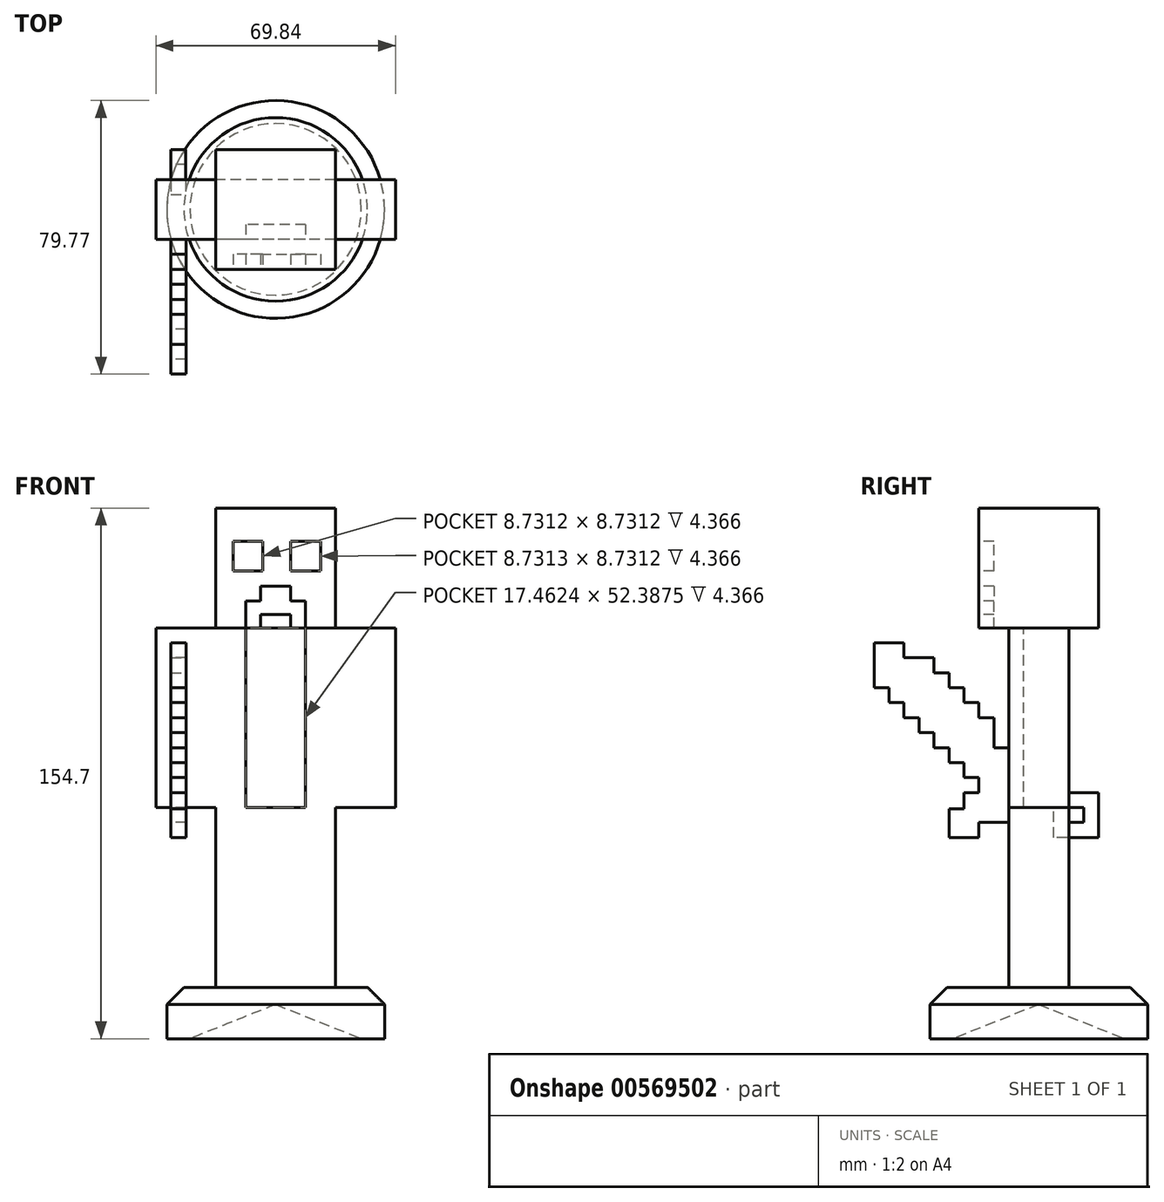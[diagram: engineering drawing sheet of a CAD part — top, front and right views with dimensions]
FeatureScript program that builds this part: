
annotation { "Feature Type Name" : "Feature", "Feature Type Description" : "" }
export const myFeature = defineFeature(function(context is Context, id is Id, definition is map)
    precondition{}
    {
        {
            var Q0;
            Q0=qCreatedBy(makeId("Top.planeOp"),FACE);
            var sketch = newSketch(context, id + "F0", { "sketchPlane" : qUnion([Q0])});
            skCircle(sketch, "E0", {"center": v(0, 0) * mm, "radius": 31.75 * mm});
            skSolve(sketch);
        }
        {
            var Q0;
            Q0=makeQuery(id+"F0.imprint","IMPRINT",FACE,{"disambiguationData":[TD([[makeQuery(id+"F0.imprint","IMPRINT",EDGE,{"derivedFrom":sQuery(id+"F0.wireOp",EDGE,"E0")}),1.0]])]});
            extrude(context, id + "F1", {"entities" : qUnion([Q0]), "depth" : 15 * mm});
        }
        {
            var Q0;
            Q0=makeQuery(id+"F1.opExtrude","CAP_EDGE",EDGE,{"disambiguationData":[OSD([sQuery(id+"F0.wireOp",EDGE,"E0")])],"isStart":false});
            chamfer(context, id + "F2", {"entities" : qUnion([Q0]), "width" : 5 * mm, "tangentPropagation" : true});
        }
        {
            var Q0;
            Q0=makeQuery(id+"F1.opExtrude","CAP_FACE",FACE,{"disambiguationData":[OSD([sQuery(id+"F0.wireOp",EDGE,"E0")])],"isStart":true});
            var sketch = newSketch(context, id + "F3", { "sketchPlane" : qUnion([Q0])});
            skCircle(sketch, "E1", {"center": v(0, 0) * mm, "radius": 25 * mm});
            skSolve(sketch);
        }
        {
            var Q0;
            Q0=makeQuery(id+"F3.imprint","IMPRINT",FACE,{"disambiguationData":[TD([[makeQuery(id+"F3.imprint","IMPRINT",EDGE,{"derivedFrom":sQuery(id+"F3.wireOp",EDGE,"E1")}),1.0]])]});
            extrude(context, id + "F4", {"entities" : qUnion([Q0]), "operationType" : NewBodyOperationType.REMOVE, "oppositeDirection" : true, "depth" : 10 * mm});
        }
        {
            var Q0;
            Q0=makeQuery(id+"F4.boolean.opBoolean","COPY",EDGE,{"derivedFrom":makeQuery(id+"F4.opExtrude","CAP_EDGE",EDGE,{"disambiguationData":[OSD([sQuery(id+"F3.wireOp",EDGE,"E1")])],"isStart":false})});
            chamfer(context, id + "F5", {"entities" : qUnion([Q0]), "chamferType" : ChamferType.TWO_OFFSETS, "width1" : 25 * mm, "oppositeDirection" : false, "width2" : 10 * mm, "tangentPropagation" : true});
        }
        {
            var Q0;
            Q0=makeQuery(id+"F1.opExtrude","CAP_FACE",FACE,{"disambiguationData":[OSD([sQuery(id+"F0.wireOp",EDGE,"E0")])],"isStart":false});
            var sketch = newSketch(context, id + "F6", { "sketchPlane" : qUnion([Q0])});
            skLineSegment(sketch, "E2.bottom", {"start": v(17.46, 8.73) * mm, "end": v(-17.46, 8.73) * mm});
            skLineSegment(sketch, "E2.top", {"start": v(17.46, -8.73) * mm, "end": v(-17.46, -8.73) * mm});
            skLineSegment(sketch, "E2.left", {"start": v(17.46, 8.73) * mm, "end": v(17.46, -8.73) * mm});
            skLineSegment(sketch, "E2.right", {"start": v(-17.46, 8.73) * mm, "end": v(-17.46, -8.73) * mm});
            skPoint(sketch, "E2.middle", {"position": v(0, 0) * mm});
            skSolve(sketch);
        }
        {
            var Q0;
            Q0=makeQuery(id+"F6.imprint","IMPRINT",FACE,{"disambiguationData":[TD([[makeQuery(id+"F6.imprint","IMPRINT",EDGE,{"derivedFrom":sQuery(id+"F6.wireOp",EDGE,"E2.bottom")}),1.0]])]});
            extrude(context, id + "F7", {"entities" : qUnion([Q0]), "operationType" : NewBodyOperationType.ADD, "depth" : 104.77 * mm});
        }
        {
            var Q0;
            Q0=makeQuery(id+"F7.opExtrude","SWEPT_FACE",FACE,{"disambiguationData":[OSD([sQuery(id+"F6.wireOp",EDGE,"E2.right")])]});
            var sketch = newSketch(context, id + "F8", { "sketchPlane" : qUnion([Q0])});
            skSolve(sketch);
        }
        {
            var Q0;
            Q0=makeQuery(id+"F7.opExtrude","SWEPT_FACE",FACE,{"disambiguationData":[OSD([sQuery(id+"F6.wireOp",EDGE,"E2.top")])]});
            var sketch = newSketch(context, id + "F9", { "sketchPlane" : qUnion([Q0])});
            skLineSegment(sketch, "E3", {"start": v(-17.46, 119.77) * mm, "end": v(17.46, 119.77) * mm});
            skSolve(sketch);
        }
        {
            var Q0;
            Q0=makeQuery(id+"F7.opExtrude","CAP_FACE",FACE,{"disambiguationData":[OSD([sQuery(id+"F6.wireOp",EDGE,"E2.bottom"),sQuery(id+"F6.wireOp",EDGE,"E2.top"),sQuery(id+"F6.wireOp",EDGE,"E2.left"),sQuery(id+"F6.wireOp",EDGE,"E2.right")])],"isStart":false});
            var sketch = newSketch(context, id + "F10", { "sketchPlane" : qUnion([Q0])});
            skLineSegment(sketch, "E4.bottom", {"start": v(17.46, -17.46) * mm, "end": v(-17.46, -17.46) * mm});
            skLineSegment(sketch, "E4.top", {"start": v(17.46, 17.46) * mm, "end": v(-17.46, 17.46) * mm});
            skLineSegment(sketch, "E4.left", {"start": v(17.46, -17.46) * mm, "end": v(17.46, 17.46) * mm});
            skLineSegment(sketch, "E4.right", {"start": v(-17.46, -17.46) * mm, "end": v(-17.46, 17.46) * mm});
            skPoint(sketch, "E4.middle", {"position": v(0, 0) * mm});
            skSolve(sketch);
        }
        {
            var Q0;
            Q0=qSketchRegion(id+"F10",true);
            extrude(context, id + "F11", {"entities" : qUnion([Q0]), "operationType" : NewBodyOperationType.ADD, "depth" : 34.92 * mm});
        }
        {
            var Q0;
            Q0=makeQuery(id+"F11.boolean.opBoolean","MERGE",FACE,{"derivedFrom":[makeQuery(id+"F7.opExtrude","SWEPT_FACE",FACE,{"disambiguationData":[OSD([sQuery(id+"F6.wireOp",EDGE,"E2.left")])]}),makeQuery(id+"F11.opExtrude","SWEPT_FACE",FACE,{"disambiguationData":[OSD([sQuery(id+"F10.wireOp",EDGE,"E4.left")])]})]});
            var sketch = newSketch(context, id + "F12", { "sketchPlane" : qUnion([Q0])});
            skLineSegment(sketch, "E5.bottom", {"start": v(-8.73, 119.77) * mm, "end": v(8.73, 119.77) * mm});
            skLineSegment(sketch, "E5.top", {"start": v(-8.73, 102.31) * mm, "end": v(8.73, 102.31) * mm});
            skLineSegment(sketch, "E5.left", {"start": v(-8.73, 119.77) * mm, "end": v(-8.73, 102.31) * mm});
            skLineSegment(sketch, "E5.right", {"start": v(8.73, 119.77) * mm, "end": v(8.73, 102.31) * mm});
            skSolve(sketch);
        }
        {
            var Q0;
            Q0=makeQuery(id+"F12.imprint","IMPRINT",FACE,{"disambiguationData":[TD([[makeQuery(id+"F12.imprint","IMPRINT",EDGE,{"derivedFrom":sQuery(id+"F12.wireOp",EDGE,"E5.bottom")}),-1.0]])]});
            extrude(context, id + "F13", {"entities" : qUnion([Q0]), "operationType" : NewBodyOperationType.ADD, "depth" : 17.46 * mm});
        }
        {
            var Q0;
            Q0=makeQuery(id+"F13.opExtrude","SWEPT_FACE",FACE,{"disambiguationData":[OSD([sQuery(id+"F12.wireOp",EDGE,"E5.top")])]});
            extrude(context, id + "F14", {"entities" : qUnion([Q0]), "operationType" : NewBodyOperationType.ADD, "depth" : 34.92 * mm});
        }
        {
            var Q0;
            {var subQ0=sQuery(id+"F6.wireOp",EDGE,"E2.right");Q0=makeQuery(id+"F8.imprint","IMPRINT",FACE,{"disambiguationData":[TD([[makeQuery(id+"F8.imprint","IMPRINT",EDGE,{"derivedFrom":makeQuery(id+"F7.opExtrude","CAP_EDGE",EDGE,{"disambiguationData":[OSD([subQ0])],"isStart":false})}),-1.0]])]});}
            var sketch = newSketch(context, id + "F15", { "sketchPlane" : qUnion([Q0])});
            skLineSegment(sketch, "E6.bottom", {"start": v(-8.73, 119.77) * mm, "end": v(8.73, 119.77) * mm});
            skLineSegment(sketch, "E6.top", {"start": v(-8.73, 102.31) * mm, "end": v(8.73, 102.31) * mm});
            skLineSegment(sketch, "E6.left", {"start": v(-8.73, 119.77) * mm, "end": v(-8.73, 102.31) * mm});
            skLineSegment(sketch, "E6.right", {"start": v(8.73, 119.77) * mm, "end": v(8.73, 102.31) * mm});
            skLineSegment(sketch, "E7", {"start": v(8.73, 102.31) * mm, "end": v(-8.73, 102.31) * mm});
            skLineSegment(sketch, "E8", {"start": v(-8.73, 102.31) * mm, "end": v(-8.73, 67.39) * mm});
            skLineSegment(sketch, "E9", {"start": v(-8.73, 67.39) * mm, "end": v(8.73, 67.39) * mm});
            skLineSegment(sketch, "E10", {"start": v(8.73, 67.39) * mm, "end": v(8.73, 102.31) * mm});
            skSolve(sketch);
        }
        {
            var Q0;
            Q0=qSketchRegion(id+"F15",true);
            extrude(context, id + "F16", {"entities" : qUnion([Q0]), "operationType" : NewBodyOperationType.ADD, "depth" : 17.46 * mm});
        }
        {
            var Q0;
            {var subQ0=sQuery(id+"F12.wireOp",EDGE,"E5.right");var subQ1=sQuery(id+"F6.wireOp",EDGE,"E2.bottom");Q0=makeQuery(id+"F16.boolean.opBoolean","MERGE",FACE,{"derivedFrom":[makeQuery(id+"F14.boolean.opBoolean","MERGE",FACE,{"derivedFrom":[makeQuery(id+"F13.boolean.opBoolean","MERGE",FACE,{"derivedFrom":[makeQuery(id+"F7.opExtrude","SWEPT_FACE",FACE,{"disambiguationData":[OSD([subQ1])]}),makeQuery(id+"F13.opExtrude","SWEPT_FACE",FACE,{"disambiguationData":[OSD([subQ0])]})]}),makeQuery(id+"F14.opExtrude","SWEPT_FACE",FACE,{"disambiguationData":[OSD([subQ1,sQuery(id+"F6.wireOp",EDGE,"E2.left"),sQuery(id+"F12.wireOp",EDGE,"E5.top"),subQ0])]})]}),makeQuery(id+"F16.opExtrude","SWEPT_FACE",FACE,{"disambiguationData":[OSD([sQuery(id+"F15.wireOp",EDGE,"E6.left"),sQuery(id+"F15.wireOp",EDGE,"E8")])]})]});}
            var sketch = newSketch(context, id + "F17", { "sketchPlane" : qUnion([Q0])});
            skLineSegment(sketch, "E11", {"start": v(-17.46, 119.77) * mm, "end": v(-17.46, 67.39) * mm});
            skLineSegment(sketch, "E12", {"start": v(-17.46, 67.39) * mm, "end": v(17.46, 67.39) * mm});
            skLineSegment(sketch, "E13", {"start": v(17.46, 67.39) * mm, "end": v(17.46, 119.77) * mm});
            skLineSegment(sketch, "E14", {"start": v(17.46, 119.77) * mm, "end": v(17.46, 67.39) * mm});
            skLineSegment(sketch, "E15", {"start": v(0, 67.39) * mm, "end": v(0, 15) * mm});
            skLineSegment(sketch, "E16", {"start": v(0, 15) * mm, "end": v(0, 67.39) * mm});
            skLineSegment(sketch, "E17", {"start": v(17.46, 119.77) * mm, "end": v(-17.46, 119.77) * mm});
            skLineSegment(sketch, "E18", {"start": v(26.2, 67.39) * mm, "end": v(26.2, 71.75) * mm});
            skLineSegment(sketch, "E19", {"start": v(26.2, 71.75) * mm, "end": v(30.56, 71.75) * mm});
            skLineSegment(sketch, "E20", {"start": v(30.56, 71.75) * mm, "end": v(30.56, 67.39) * mm});
            skLineSegment(sketch, "E21", {"start": v(30.56, 67.39) * mm, "end": v(26.2, 67.39) * mm});
            skSolve(sketch);
        }
        {
            var Q0;
            Q0=makeQuery(id+"F9.imprint","IMPRINT",FACE,{"disambiguationData":[TD([[makeQuery(id+"F9.imprint","IMPRINT",EDGE,{"derivedFrom":sQuery(id+"F9.wireOp",EDGE,"E3")}),1.0]])]});
            var sketch = newSketch(context, id + "F18", { "sketchPlane" : qUnion([Q0])});
            skLineSegment(sketch, "E22", {"start": v(-17.46, 67.39) * mm, "end": v(17.46, 67.39) * mm});
            skLineSegment(sketch, "E23", {"start": v(17.46, 67.39) * mm, "end": v(17.46, 119.77) * mm});
            skLineSegment(sketch, "E24", {"start": v(17.46, 119.77) * mm, "end": v(-17.46, 119.77) * mm});
            skLineSegment(sketch, "E25", {"start": v(-17.46, 119.77) * mm, "end": v(-17.46, 67.39) * mm});
            skLineSegment(sketch, "E26", {"start": v(0, 67.39) * mm, "end": v(0, 15) * mm});
            skLineSegment(sketch, "E27", {"start": v(0, 15) * mm, "end": v(0, 67.39) * mm});
            skLineSegment(sketch, "E28", {"start": v(17.46, 67.39) * mm, "end": v(-17.46, 67.39) * mm});
            skSolve(sketch);
        }
        {
            var Q0;
            Q0=makeQuery(id+"F11.opExtrude","SWEPT_FACE",FACE,{"disambiguationData":[OSD([sQuery(id+"F10.wireOp",EDGE,"E4.bottom")])]});
            var sketch = newSketch(context, id + "F19", { "sketchPlane" : qUnion([Q0])});
            skLineSegment(sketch, "E29", {"start": v(-8.73, 119.77) * mm, "end": v(-8.73, 127.59) * mm});
            skLineSegment(sketch, "E30", {"start": v(-8.73, 127.59) * mm, "end": v(-4.37, 127.59) * mm});
            skLineSegment(sketch, "E31", {"start": v(-4.37, 127.59) * mm, "end": v(-4.37, 131.95) * mm});
            skLineSegment(sketch, "E32", {"start": v(-4.37, 131.95) * mm, "end": v(4.37, 131.95) * mm});
            skLineSegment(sketch, "E33", {"start": v(4.37, 131.95) * mm, "end": v(4.37, 127.59) * mm});
            skLineSegment(sketch, "E34", {"start": v(4.37, 127.59) * mm, "end": v(8.73, 127.59) * mm});
            skLineSegment(sketch, "E35", {"start": v(8.73, 127.59) * mm, "end": v(8.73, 119.77) * mm});
            skLineSegment(sketch, "E36", {"start": v(-8.73, 119.77) * mm, "end": v(-4.37, 119.77) * mm});
            skLineSegment(sketch, "E37", {"start": v(-4.37, 119.77) * mm, "end": v(-4.37, 123.68) * mm});
            skPoint(sketch, "E37.endSnap0", {"position": v(-8.73, 123.68) * mm});
            skLineSegment(sketch, "E38", {"start": v(-4.37, 123.68) * mm, "end": v(4.37, 123.68) * mm});
            skLineSegment(sketch, "E39", {"start": v(4.37, 123.68) * mm, "end": v(4.37, 119.77) * mm});
            skLineSegment(sketch, "E40", {"start": v(4.37, 119.77) * mm, "end": v(8.73, 119.77) * mm});
            skLineSegment(sketch, "E41.bottom", {"start": v(-3.7, 136.32) * mm, "end": v(-12.43, 136.32) * mm});
            skLineSegment(sketch, "E41.top", {"start": v(-3.7, 145.05) * mm, "end": v(-12.43, 145.05) * mm});
            skLineSegment(sketch, "E41.left", {"start": v(-3.7, 136.32) * mm, "end": v(-3.7, 145.05) * mm});
            skLineSegment(sketch, "E41.right", {"start": v(-12.43, 136.32) * mm, "end": v(-12.43, 145.05) * mm});
            skPoint(sketch, "E42.oppositeSnap0", {"position": v(-8.07, 145.05) * mm});
            skLineSegment(sketch, "E42.bottom", {"start": v(4.37, 136.32) * mm, "end": v(13.1, 136.32) * mm});
            skLineSegment(sketch, "E42.top", {"start": v(4.37, 145.05) * mm, "end": v(13.1, 145.05) * mm});
            skLineSegment(sketch, "E42.left", {"start": v(4.37, 136.32) * mm, "end": v(4.37, 145.05) * mm});
            skLineSegment(sketch, "E42.right", {"start": v(13.1, 136.32) * mm, "end": v(13.1, 145.05) * mm});
            skSolve(sketch);
        }
        {
            var Q0;
            Q0=qSketchRegion(id+"F19",true);
            extrude(context, id + "F20", {"entities" : qUnion([Q0]), "operationType" : NewBodyOperationType.REMOVE, "oppositeDirection" : true, "depth" : 4.37 * mm});
        }
        {
            var Q0;
            Q0=makeQuery(id+"F9.imprint","IMPRINT",FACE,{"disambiguationData":[TD([[makeQuery(id+"F9.imprint","IMPRINT",EDGE,{"derivedFrom":sQuery(id+"F9.wireOp",EDGE,"E3")}),1.0]])]});
            var sketch = newSketch(context, id + "F21", { "sketchPlane" : qUnion([Q0])});
            skLineSegment(sketch, "E43", {"start": v(-8.73, 67.39) * mm, "end": v(-8.73, 119.77) * mm});
            skLineSegment(sketch, "E44", {"start": v(-8.73, 119.77) * mm, "end": v(8.73, 119.77) * mm});
            skLineSegment(sketch, "E45", {"start": v(8.73, 119.77) * mm, "end": v(8.73, 67.39) * mm});
            skLineSegment(sketch, "E46", {"start": v(8.73, 67.39) * mm, "end": v(-8.73, 67.39) * mm});
            skSolve(sketch);
        }
        {
            var Q0;
            Q0=makeQuery(id+"F17.imprint","IMPRINT",FACE,{"disambiguationData":[TD([[makeQuery(id+"F17.imprint","IMPRINT",EDGE,{"derivedFrom":sQuery(id+"F17.wireOp",EDGE,"E18")}),-1.0]])]});
            var sketch = newSketch(context, id + "F22", { "sketchPlane" : qUnion([Q0])});
            skSolve(sketch);
        }
        {
            var Q0;
            Q0=qSketchRegion(id+"F22",true);
            var Q1;
            Q1=makeQuery(id+"F17.imprint","IMPRINT",FACE,{"disambiguationData":[TD([[makeQuery(id+"F17.imprint","IMPRINT",EDGE,{"derivedFrom":sQuery(id+"F17.wireOp",EDGE,"E18")}),-1.0]])]});
            extrude(context, id + "F23", {"entities" : qUnion([Q0, Q1]), "operationType" : NewBodyOperationType.ADD, "depth" : 4.37 * mm});
        }
        {
            var Q0;
            Q0=makeQuery(id+"F23.opExtrude","SWEPT_FACE",FACE,{"disambiguationData":[OSD([sQuery(id+"F17.wireOp",EDGE,"E19")])]});
            extrude(context, id + "F24", {"entities" : qUnion([Q0]), "operationType" : NewBodyOperationType.ADD, "depth" : 4.37 * mm});
        }
        {
            var Q0;
            {var subQ0=sQuery(id+"F12.wireOp",EDGE,"E5.left");var subQ1=sQuery(id+"F6.wireOp",EDGE,"E2.top");Q0=makeQuery(id+"F16.boolean.opBoolean","MERGE",FACE,{"derivedFrom":[makeQuery(id+"F14.boolean.opBoolean","MERGE",FACE,{"derivedFrom":[makeQuery(id+"F13.boolean.opBoolean","MERGE",FACE,{"derivedFrom":[makeQuery(id+"F7.opExtrude","SWEPT_FACE",FACE,{"disambiguationData":[OSD([subQ1])]}),makeQuery(id+"F13.opExtrude","SWEPT_FACE",FACE,{"disambiguationData":[OSD([subQ0])]})]}),makeQuery(id+"F14.opExtrude","SWEPT_FACE",FACE,{"disambiguationData":[OSD([subQ1,sQuery(id+"F6.wireOp",EDGE,"E2.left"),sQuery(id+"F12.wireOp",EDGE,"E5.top"),subQ0])]})]}),makeQuery(id+"F16.opExtrude","SWEPT_FACE",FACE,{"disambiguationData":[OSD([sQuery(id+"F15.wireOp",EDGE,"E6.right"),sQuery(id+"F15.wireOp",EDGE,"E10")])]})]});}
            var sketch = newSketch(context, id + "F25", { "sketchPlane" : qUnion([Q0])});
            skLineSegment(sketch, "E47", {"start": v(-34.92, 67.39) * mm, "end": v(-17.46, 67.39) * mm});
            skLineSegment(sketch, "E48", {"start": v(-17.46, 67.39) * mm, "end": v(-17.46, 119.77) * mm});
            skLineSegment(sketch, "E49", {"start": v(-17.46, 119.77) * mm, "end": v(-34.92, 119.77) * mm});
            skLineSegment(sketch, "E50", {"start": v(-34.92, 119.77) * mm, "end": v(-34.92, 67.39) * mm});
            skLineSegment(sketch, "E51", {"start": v(-30.56, 67.39) * mm, "end": v(-30.56, 71.75) * mm});
            skLineSegment(sketch, "E52", {"start": v(-30.56, 71.75) * mm, "end": v(-26.16, 71.75) * mm});
            skLineSegment(sketch, "E53", {"start": v(-26.16, 71.75) * mm, "end": v(-26.16, 67.39) * mm});
            skLineSegment(sketch, "E54", {"start": v(-26.16, 67.39) * mm, "end": v(-30.56, 67.39) * mm});
            skSolve(sketch);
        }
        {
            var Q0;
            Q0=makeQuery(id+"F25.imprint","IMPRINT",FACE,{"disambiguationData":[TD([[makeQuery(id+"F25.imprint","IMPRINT",EDGE,{"derivedFrom":sQuery(id+"F25.wireOp",EDGE,"E51")}),-1.0]])]});
            extrude(context, id + "F26", {"entities" : qUnion([Q0]), "operationType" : NewBodyOperationType.ADD, "depth" : 4.37 * mm});
        }
        {
            var Q0;
            Q0=makeQuery(id+"F26.opExtrude","SWEPT_FACE",FACE,{"disambiguationData":[OSD([sQuery(id+"F25.wireOp",EDGE,"E52")])]});
            extrude(context, id + "F27", {"entities" : qUnion([Q0]), "operationType" : NewBodyOperationType.ADD, "depth" : 8.73 * mm});
        }
        {
            var Q0;
            {var subQ0=sQuery(id+"F25.wireOp",EDGE,"E52");Q0=makeQuery(id+"F27.boolean.opBoolean","MERGE",FACE,{"derivedFrom":[makeQuery(id+"F26.opExtrude","CAP_FACE",FACE,{"disambiguationData":[OSD([sQuery(id+"F25.wireOp",EDGE,"E51"),subQ0,sQuery(id+"F25.wireOp",EDGE,"E53"),sQuery(id+"F25.wireOp",EDGE,"E54")])],"isStart":false}),makeQuery(id+"F27.opExtrude","SWEPT_FACE",FACE,{"disambiguationData":[OSD([subQ0]),TDD([makeQuery(id+"F26.opExtrude","CAP_EDGE",EDGE,{"disambiguationData":[OSD([subQ0])],"isStart":false})])]})]});}
            var sketch = newSketch(context, id + "F28", { "sketchPlane" : qUnion([Q0])});
            skLineSegment(sketch, "E55", {"start": v(-30.56, 71.75) * mm, "end": v(-26.16, 71.75) * mm});
            skLineSegment(sketch, "E56", {"start": v(-30.56, 76.12) * mm, "end": v(-26.16, 76.12) * mm});
            skSolve(sketch);
        }
        {
            var Q0;
            Q0=qSketchRegion(id+"F28",true);
            var Q1;
            {var subQ0=sQuery(id+"F28.wireOp",EDGE,"E55");Q1=makeQuery(id+"F28.imprint","IMPRINT",FACE,{"disambiguationData":[TD([[makeQuery(id+"F28.imprint","IMPRINT",EDGE,{"derivedFrom":subQ0}),1.0]])]});}
            var Q2;
            {var subQ0=sQuery(id+"F28.wireOp",EDGE,"E56");Q2=makeQuery(id+"F28.imprint","IMPRINT",FACE,{"disambiguationData":[TD([[makeQuery(id+"F28.imprint","IMPRINT",EDGE,{"derivedFrom":subQ0}),1.0]])]});}
            extrude(context, id + "F29", {"entities" : qUnion([Q0, Q1, Q2]), "operationType" : NewBodyOperationType.ADD, "depth" : 4.37 * mm});
        }
        {
            var Q0;
            {var subQ0=sQuery(id+"F25.wireOp",EDGE,"E52");Q0=makeQuery(id+"F29.boolean.opBoolean","MERGE",FACE,{"derivedFrom":[makeQuery(id+"F27.opExtrude","CAP_FACE",FACE,{"disambiguationData":[OSD([subQ0])],"isStart":false}),makeQuery(id+"F29.opExtrude","SWEPT_FACE",FACE,{"disambiguationData":[OSD([subQ0])]})]});}
            var sketch = newSketch(context, id + "F30", { "sketchPlane" : qUnion([Q0])});
            skLineSegment(sketch, "E57", {"start": v(-26.16, -13.1) * mm, "end": v(-30.56, -13.1) * mm});
            skSolve(sketch);
        }
        {
            var Q0;
            Q0=qSketchRegion(id+"F30",true);
            var Q1;
            {var subQ0=sQuery(id+"F30.wireOp",EDGE,"E57");Q1=makeQuery(id+"F30.imprint","IMPRINT",FACE,{"disambiguationData":[TD([[makeQuery(id+"F30.imprint","IMPRINT",EDGE,{"derivedFrom":subQ0}),1.0]])]});}
            extrude(context, id + "F31", {"entities" : qUnion([Q0, Q1]), "operationType" : NewBodyOperationType.ADD, "depth" : 4.37 * mm});
        }
        {
            var Q0;
            {var subQ0=sQuery(id+"F25.wireOp",EDGE,"E52");Q0=makeQuery(id+"F31.boolean.opBoolean","MERGE",FACE,{"derivedFrom":[makeQuery(id+"F29.opExtrude","CAP_FACE",FACE,{"disambiguationData":[OSD([sQuery(id+"F25.wireOp",EDGE,"E51"),subQ0,sQuery(id+"F25.wireOp",EDGE,"E53"),sQuery(id+"F28.wireOp",EDGE,"E55")])],"isStart":false}),makeQuery(id+"F31.opExtrude","SWEPT_FACE",FACE,{"disambiguationData":[OSD([subQ0])]})]});}
            var sketch = newSketch(context, id + "F32", { "sketchPlane" : qUnion([Q0])});
            skLineSegment(sketch, "E58", {"start": v(-30.56, 80.48) * mm, "end": v(-26.16, 80.48) * mm});
            skPoint(sketch, "E58.endSnap0", {"position": v(-26.16, 78.3) * mm});
            skLineSegment(sketch, "E59", {"start": v(-26.16, 80.48) * mm, "end": v(-26.16, 76.12) * mm});
            skLineSegment(sketch, "E60", {"start": v(-26.16, 76.12) * mm, "end": v(-30.56, 76.12) * mm});
            skSolve(sketch);
        }
        {
            var Q0;
            Q0=qSketchRegion(id+"F32",true);
            var Q1;
            {var subQ0=sQuery(id+"F32.wireOp",EDGE,"E58");Q1=makeQuery(id+"F32.imprint","IMPRINT",FACE,{"disambiguationData":[TD([[makeQuery(id+"F32.imprint","IMPRINT",EDGE,{"derivedFrom":subQ0}),-1.0]])]});}
            extrude(context, id + "F33", {"entities" : qUnion([Q0, Q1]), "operationType" : NewBodyOperationType.ADD, "depth" : 4.37 * mm});
        }
        {
            var Q0;
            Q0=makeQuery(id+"F33.opExtrude","SWEPT_FACE",FACE,{"disambiguationData":[OSD([sQuery(id+"F32.wireOp",EDGE,"E58")])]});
            extrude(context, id + "F34", {"entities" : qUnion([Q0]), "operationType" : NewBodyOperationType.ADD, "depth" : 8.73 * mm});
        }
        {
            var Q0;
            {var subQ0=sQuery(id+"F32.wireOp",EDGE,"E58");Q0=makeQuery(id+"F34.boolean.opBoolean","MERGE",FACE,{"derivedFrom":[makeQuery(id+"F33.opExtrude","CAP_FACE",FACE,{"disambiguationData":[OSD([sQuery(id+"F25.wireOp",EDGE,"E51"),sQuery(id+"F25.wireOp",EDGE,"E52"),subQ0,sQuery(id+"F32.wireOp",EDGE,"E59"),sQuery(id+"F32.wireOp",EDGE,"E60")])],"isStart":false}),makeQuery(id+"F34.opExtrude","SWEPT_FACE",FACE,{"disambiguationData":[OSD([subQ0]),TDD([makeQuery(id+"F33.opExtrude","CAP_EDGE",EDGE,{"disambiguationData":[OSD([subQ0])],"isStart":false})])]})]});}
            var sketch = newSketch(context, id + "F35", { "sketchPlane" : qUnion([Q0])});
            skLineSegment(sketch, "E61", {"start": v(-30.56, 80.48) * mm, "end": v(-26.16, 80.48) * mm});
            skLineSegment(sketch, "E62", {"start": v(-26.16, 80.48) * mm, "end": v(-26.16, 84.85) * mm});
            skLineSegment(sketch, "E63", {"start": v(-26.16, 84.85) * mm, "end": v(-30.56, 84.85) * mm});
            skSolve(sketch);
        }
        {
            var Q0;
            Q0=qSketchRegion(id+"F35",true);
            var Q1;
            {var subQ0=sQuery(id+"F35.wireOp",EDGE,"E61");Q1=makeQuery(id+"F35.imprint","IMPRINT",FACE,{"disambiguationData":[TD([[makeQuery(id+"F35.imprint","IMPRINT",EDGE,{"derivedFrom":subQ0}),1.0]])]});}
            extrude(context, id + "F36", {"entities" : qUnion([Q0, Q1]), "operationType" : NewBodyOperationType.ADD, "depth" : 4.37 * mm});
        }
        {
            var Q0;
            Q0=makeQuery(id+"F36.opExtrude","SWEPT_FACE",FACE,{"disambiguationData":[OSD([sQuery(id+"F35.wireOp",EDGE,"E63")])]});
            extrude(context, id + "F37", {"entities" : qUnion([Q0]), "operationType" : NewBodyOperationType.ADD, "depth" : 8.73 * mm});
        }
        {
            var Q0;
            {var subQ0=sQuery(id+"F35.wireOp",EDGE,"E63");Q0=makeQuery(id+"F37.boolean.opBoolean","MERGE",FACE,{"derivedFrom":[makeQuery(id+"F36.opExtrude","CAP_FACE",FACE,{"disambiguationData":[OSD([sQuery(id+"F25.wireOp",EDGE,"E51"),sQuery(id+"F25.wireOp",EDGE,"E52"),sQuery(id+"F32.wireOp",EDGE,"E58"),sQuery(id+"F35.wireOp",EDGE,"E61"),sQuery(id+"F35.wireOp",EDGE,"E62"),subQ0])],"isStart":false}),makeQuery(id+"F37.opExtrude","SWEPT_FACE",FACE,{"disambiguationData":[OSD([subQ0]),TDD([makeQuery(id+"F36.opExtrude","CAP_EDGE",EDGE,{"disambiguationData":[OSD([subQ0])],"isStart":false})])]})]});}
            var sketch = newSketch(context, id + "F38", { "sketchPlane" : qUnion([Q0])});
            skLineSegment(sketch, "E64", {"start": v(-30.56, 84.85) * mm, "end": v(-26.16, 84.85) * mm});
            skLineSegment(sketch, "E65", {"start": v(-26.16, 84.85) * mm, "end": v(-26.16, 89.21) * mm});
            skLineSegment(sketch, "E66", {"start": v(-26.16, 89.21) * mm, "end": v(-30.56, 89.21) * mm});
            skSolve(sketch);
        }
        {
            var Q0;
            Q0=qSketchRegion(id+"F38",true);
            var Q1;
            {var subQ0=sQuery(id+"F38.wireOp",EDGE,"E64");Q1=makeQuery(id+"F38.imprint","IMPRINT",FACE,{"disambiguationData":[TD([[makeQuery(id+"F38.imprint","IMPRINT",EDGE,{"derivedFrom":subQ0}),1.0]])]});}
            extrude(context, id + "F39", {"entities" : qUnion([Q0, Q1]), "operationType" : NewBodyOperationType.ADD, "depth" : 4.37 * mm});
        }
        {
            var Q0;
            Q0=makeQuery(id+"F39.opExtrude","SWEPT_FACE",FACE,{"disambiguationData":[OSD([sQuery(id+"F38.wireOp",EDGE,"E66")])]});
            extrude(context, id + "F40", {"entities" : qUnion([Q0]), "operationType" : NewBodyOperationType.ADD, "depth" : 8.73 * mm});
        }
        {
            var Q0;
            {var subQ0=sQuery(id+"F38.wireOp",EDGE,"E66");Q0=makeQuery(id+"F40.boolean.opBoolean","MERGE",FACE,{"derivedFrom":[makeQuery(id+"F39.opExtrude","CAP_FACE",FACE,{"disambiguationData":[OSD([sQuery(id+"F25.wireOp",EDGE,"E51"),sQuery(id+"F25.wireOp",EDGE,"E52"),sQuery(id+"F32.wireOp",EDGE,"E58"),sQuery(id+"F35.wireOp",EDGE,"E63"),sQuery(id+"F38.wireOp",EDGE,"E64"),sQuery(id+"F38.wireOp",EDGE,"E65"),subQ0])],"isStart":false}),makeQuery(id+"F40.opExtrude","SWEPT_FACE",FACE,{"disambiguationData":[OSD([subQ0]),TDD([makeQuery(id+"F39.opExtrude","CAP_EDGE",EDGE,{"disambiguationData":[OSD([subQ0])],"isStart":false})])]})]});}
            var sketch = newSketch(context, id + "F41", { "sketchPlane" : qUnion([Q0])});
            skLineSegment(sketch, "E67", {"start": v(-30.56, 93.58) * mm, "end": v(-26.16, 93.58) * mm});
            skLineSegment(sketch, "E68", {"start": v(-26.16, 93.58) * mm, "end": v(-26.16, 89.22) * mm});
            skLineSegment(sketch, "E69", {"start": v(-26.16, 89.22) * mm, "end": v(-30.56, 89.22) * mm});
            skSolve(sketch);
        }
        {
            var Q0;
            {var subQ0=sQuery(id+"F17.wireOp",EDGE,"E19");Q0=makeQuery(id+"F24.boolean.opBoolean","MERGE",FACE,{"derivedFrom":[makeQuery(id+"F23.opExtrude","CAP_FACE",FACE,{"disambiguationData":[OSD([sQuery(id+"F17.wireOp",EDGE,"E18"),subQ0,sQuery(id+"F17.wireOp",EDGE,"E20"),sQuery(id+"F17.wireOp",EDGE,"E21")])],"isStart":false}),makeQuery(id+"F24.opExtrude","SWEPT_FACE",FACE,{"disambiguationData":[OSD([subQ0]),TDD([makeQuery(id+"F23.opExtrude","CAP_EDGE",EDGE,{"disambiguationData":[OSD([subQ0])],"isStart":false})])]})]});}
            var sketch = newSketch(context, id + "F42", { "sketchPlane" : qUnion([Q0])});
            skLineSegment(sketch, "E70", {"start": v(26.2, 71.75) * mm, "end": v(30.56, 71.75) * mm});
            skSolve(sketch);
        }
        {
            var Q0;
            {var subQ0=sQuery(id+"F42.wireOp",EDGE,"E70");Q0=makeQuery(id+"F42.imprint","IMPRINT",FACE,{"disambiguationData":[TD([[makeQuery(id+"F42.imprint","IMPRINT",EDGE,{"derivedFrom":subQ0}),1.0]])]});}
            extrude(context, id + "F43", {"entities" : qUnion([Q0]), "operationType" : NewBodyOperationType.REMOVE, "oppositeDirection" : true, "depth" : 4.37 * mm});
        }
        {
            var Q0;
            {var subQ0=sQuery(id+"F17.wireOp",EDGE,"E19");Q0=makeQuery(id+"F24.boolean.opBoolean","MERGE",FACE,{"derivedFrom":[makeQuery(id+"F23.opExtrude","CAP_FACE",FACE,{"disambiguationData":[OSD([sQuery(id+"F17.wireOp",EDGE,"E18"),subQ0,sQuery(id+"F17.wireOp",EDGE,"E20"),sQuery(id+"F17.wireOp",EDGE,"E21")])],"isStart":false}),makeQuery(id+"F24.opExtrude","SWEPT_FACE",FACE,{"disambiguationData":[OSD([subQ0]),TDD([makeQuery(id+"F23.opExtrude","CAP_EDGE",EDGE,{"disambiguationData":[OSD([subQ0])],"isStart":false})])]})]});}
            extrude(context, id + "F44", {"entities" : qUnion([Q0]), "operationType" : NewBodyOperationType.ADD, "depth" : 4.37 * mm});
        }
        {
            var Q0;
            {var subQ0=sQuery(id+"F17.wireOp",EDGE,"E21");Q0=makeQuery(id+"F44.boolean.opBoolean","MERGE",FACE,{"derivedFrom":[makeQuery(id+"F26.boolean.opBoolean","MERGE",FACE,{"derivedFrom":[makeQuery(id+"F23.boolean.opBoolean","MERGE",FACE,{"derivedFrom":[makeQuery(id+"F16.opExtrude","SWEPT_FACE",FACE,{"disambiguationData":[OSD([sQuery(id+"F15.wireOp",EDGE,"E9")])]}),makeQuery(id+"F23.opExtrude","SWEPT_FACE",FACE,{"disambiguationData":[OSD([subQ0])]})]}),makeQuery(id+"F26.opExtrude","SWEPT_FACE",FACE,{"disambiguationData":[OSD([sQuery(id+"F25.wireOp",EDGE,"E54")])]})]}),makeQuery(id+"F44.opExtrude","SWEPT_FACE",FACE,{"disambiguationData":[OSD([subQ0])]})]});}
            var sketch = newSketch(context, id + "F45", { "sketchPlane" : qUnion([Q0])});
            skLineSegment(sketch, "E71", {"start": v(-30.56, -8.73) * mm, "end": v(-30.56, -4.37) * mm});
            skLineSegment(sketch, "E72", {"start": v(-30.56, -4.37) * mm, "end": v(-26.2, -4.37) * mm});
            skLineSegment(sketch, "E73", {"start": v(-26.2, -4.37) * mm, "end": v(-26.2, -8.73) * mm});
            skSolve(sketch);
        }
        {
            var Q0;
            Q0=qSketchRegion(id+"F45",true);
            var Q1;
            Q1=makeQuery(id+"F45.imprint","IMPRINT",FACE,{"disambiguationData":[TD([[makeQuery(id+"F45.imprint","IMPRINT",EDGE,{"derivedFrom":sQuery(id+"F45.wireOp",EDGE,"E71")}),-1.0]])]});
            extrude(context, id + "F46", {"entities" : qUnion([Q0, Q1]), "operationType" : NewBodyOperationType.ADD, "depth" : 8.73 * mm});
        }
        {
            var Q0;
            {var subQ0=sQuery(id+"F17.wireOp",EDGE,"E20");var subQ1=sQuery(id+"F17.wireOp",EDGE,"E19");Q0=makeQuery(id+"F46.boolean.opBoolean","MERGE",FACE,{"derivedFrom":[makeQuery(id+"F44.boolean.opBoolean","MERGE",FACE,{"derivedFrom":[makeQuery(id+"F24.boolean.opBoolean","MERGE",FACE,{"derivedFrom":[makeQuery(id+"F23.opExtrude","SWEPT_FACE",FACE,{"disambiguationData":[OSD([subQ0])]}),makeQuery(id+"F24.opExtrude","SWEPT_FACE",FACE,{"disambiguationData":[OSD([subQ1,subQ0])]})]}),makeQuery(id+"F44.opExtrude","SWEPT_FACE",FACE,{"disambiguationData":[OSD([subQ1,subQ0])]})]}),makeQuery(id+"F46.opExtrude","SWEPT_FACE",FACE,{"disambiguationData":[OSD([sQuery(id+"F6.wireOp",EDGE,"E2.bottom"),sQuery(id+"F6.wireOp",EDGE,"E2.right"),sQuery(id+"F15.wireOp",EDGE,"E8"),sQuery(id+"F15.wireOp",EDGE,"E9"),subQ0,sQuery(id+"F17.wireOp",EDGE,"E21"),sQuery(id+"F45.wireOp",EDGE,"E71")])]})]});}
            var sketch = newSketch(context, id + "F47", { "sketchPlane" : qUnion([Q0])});
            skLineSegment(sketch, "E74.bottom", {"start": v(-13.1, 63.02) * mm, "end": v(-8.73, 63.02) * mm});
            skLineSegment(sketch, "E74.top", {"start": v(-13.1, 67.39) * mm, "end": v(-8.73, 67.39) * mm});
            skLineSegment(sketch, "E74.left", {"start": v(-13.1, 63.02) * mm, "end": v(-13.1, 67.39) * mm});
            skLineSegment(sketch, "E74.right", {"start": v(-8.73, 63.02) * mm, "end": v(-8.73, 67.39) * mm});
            skPoint(sketch, "E74.middle", {"position": v(-10.91, 65.2) * mm});
            skPoint(sketch, "E74.middle.positionSnap0", {"position": v(-17.46, 65.2) * mm});
            skPoint(sketch, "E74.cornerSnap0", {"position": v(-4.37, 63.02) * mm});
            skPoint(sketch, "E74.centerSnap0", {"position": v(-17.46, 65.2) * mm});
            skSolve(sketch);
        }
        {
            var Q0;
            Q0=makeQuery(id+"F47.imprint","IMPRINT",FACE,{"disambiguationData":[TD([[makeQuery(id+"F47.imprint","IMPRINT",EDGE,{"derivedFrom":sQuery(id+"F47.wireOp",EDGE,"E74.bottom")}),1.0]])]});
            extrude(context, id + "F48", {"entities" : qUnion([Q0]), "operationType" : NewBodyOperationType.REMOVE, "oppositeDirection" : true, "depth" : 25 * mm});
        }
        {
            var Q0;
            {var subQ0=sQuery(id+"F41.wireOp",EDGE,"E67");Q0=makeQuery(id+"F41.imprint","IMPRINT",FACE,{"disambiguationData":[TD([[makeQuery(id+"F41.imprint","IMPRINT",EDGE,{"derivedFrom":subQ0}),-1.0]])]});}
            extrude(context, id + "F49", {"entities" : qUnion([Q0]), "operationType" : NewBodyOperationType.ADD, "depth" : 4.37 * mm});
        }
        {
            var Q0;
            Q0=makeQuery(id+"F49.opExtrude","SWEPT_FACE",FACE,{"disambiguationData":[OSD([sQuery(id+"F41.wireOp",EDGE,"E67")])]});
            extrude(context, id + "F50", {"entities" : qUnion([Q0]), "operationType" : NewBodyOperationType.ADD, "depth" : 8.73 * mm});
        }
        {
            var Q0;
            {var subQ0=sQuery(id+"F41.wireOp",EDGE,"E67");Q0=makeQuery(id+"F50.boolean.opBoolean","MERGE",FACE,{"derivedFrom":[makeQuery(id+"F49.opExtrude","CAP_FACE",FACE,{"disambiguationData":[OSD([sQuery(id+"F25.wireOp",EDGE,"E51"),sQuery(id+"F25.wireOp",EDGE,"E52"),sQuery(id+"F32.wireOp",EDGE,"E58"),sQuery(id+"F35.wireOp",EDGE,"E63"),sQuery(id+"F38.wireOp",EDGE,"E66"),subQ0,sQuery(id+"F41.wireOp",EDGE,"E68"),sQuery(id+"F41.wireOp",EDGE,"E69")])],"isStart":false}),makeQuery(id+"F50.opExtrude","SWEPT_FACE",FACE,{"disambiguationData":[OSD([subQ0]),TDD([makeQuery(id+"F49.opExtrude","CAP_EDGE",EDGE,{"disambiguationData":[OSD([subQ0])],"isStart":false})])]})]});}
            var sketch = newSketch(context, id + "F51", { "sketchPlane" : qUnion([Q0])});
            skLineSegment(sketch, "E75", {"start": v(-30.56, 97.95) * mm, "end": v(-26.16, 97.95) * mm});
            skLineSegment(sketch, "E76", {"start": v(-26.16, 97.95) * mm, "end": v(-26.16, 93.58) * mm});
            skLineSegment(sketch, "E77", {"start": v(-26.16, 93.58) * mm, "end": v(-30.56, 93.58) * mm});
            skSolve(sketch);
        }
        {
            var Q0;
            Q0=qSketchRegion(id+"F51",true);
            var Q1;
            {var subQ0=sQuery(id+"F51.wireOp",EDGE,"E75");Q1=makeQuery(id+"F51.imprint","IMPRINT",FACE,{"disambiguationData":[TD([[makeQuery(id+"F51.imprint","IMPRINT",EDGE,{"derivedFrom":subQ0}),-1.0]])]});}
            extrude(context, id + "F52", {"entities" : qUnion([Q0, Q1]), "operationType" : NewBodyOperationType.ADD, "depth" : 4.37 * mm});
        }
        {
            var Q0;
            Q0=makeQuery(id+"F52.opExtrude","SWEPT_FACE",FACE,{"disambiguationData":[OSD([sQuery(id+"F51.wireOp",EDGE,"E75")])]});
            extrude(context, id + "F53", {"entities" : qUnion([Q0]), "operationType" : NewBodyOperationType.ADD, "depth" : 8.73 * mm});
        }
        {
            var Q0;
            {var subQ0=sQuery(id+"F51.wireOp",EDGE,"E75");Q0=makeQuery(id+"F53.boolean.opBoolean","MERGE",FACE,{"derivedFrom":[makeQuery(id+"F52.opExtrude","CAP_FACE",FACE,{"disambiguationData":[OSD([sQuery(id+"F25.wireOp",EDGE,"E51"),sQuery(id+"F25.wireOp",EDGE,"E52"),sQuery(id+"F32.wireOp",EDGE,"E58"),sQuery(id+"F35.wireOp",EDGE,"E63"),sQuery(id+"F38.wireOp",EDGE,"E66"),sQuery(id+"F41.wireOp",EDGE,"E67"),subQ0,sQuery(id+"F51.wireOp",EDGE,"E76"),sQuery(id+"F51.wireOp",EDGE,"E77")])],"isStart":false}),makeQuery(id+"F53.opExtrude","SWEPT_FACE",FACE,{"disambiguationData":[OSD([subQ0]),TDD([makeQuery(id+"F52.opExtrude","CAP_EDGE",EDGE,{"disambiguationData":[OSD([subQ0])],"isStart":false})])]})]});}
            var sketch = newSketch(context, id + "F54", { "sketchPlane" : qUnion([Q0])});
            skLineSegment(sketch, "E78", {"start": v(-30.56, 102.31) * mm, "end": v(-26.16, 102.31) * mm});
            skLineSegment(sketch, "E79", {"start": v(-26.16, 102.31) * mm, "end": v(-26.16, 97.95) * mm});
            skLineSegment(sketch, "E80", {"start": v(-26.16, 97.95) * mm, "end": v(-30.56, 97.95) * mm});
            skSolve(sketch);
        }
        {
            var Q0;
            {var subQ0=sQuery(id+"F54.wireOp",EDGE,"E78");Q0=makeQuery(id+"F54.imprint","IMPRINT",FACE,{"disambiguationData":[TD([[makeQuery(id+"F54.imprint","IMPRINT",EDGE,{"derivedFrom":subQ0}),-1.0]])]});}
            extrude(context, id + "F55", {"entities" : qUnion([Q0]), "operationType" : NewBodyOperationType.ADD, "depth" : 4.37 * mm});
        }
        {
            var Q0;
            Q0=makeQuery(id+"F55.opExtrude","SWEPT_FACE",FACE,{"disambiguationData":[OSD([sQuery(id+"F54.wireOp",EDGE,"E78")])]});
            extrude(context, id + "F56", {"entities" : qUnion([Q0]), "operationType" : NewBodyOperationType.ADD, "depth" : 4.37 * mm});
        }
        {
            var Q0;
            {var subQ0=sQuery(id+"F54.wireOp",EDGE,"E78");Q0=makeQuery(id+"F56.boolean.opBoolean","MERGE",FACE,{"derivedFrom":[makeQuery(id+"F55.opExtrude","CAP_FACE",FACE,{"disambiguationData":[OSD([sQuery(id+"F25.wireOp",EDGE,"E51"),sQuery(id+"F25.wireOp",EDGE,"E52"),sQuery(id+"F32.wireOp",EDGE,"E58"),sQuery(id+"F35.wireOp",EDGE,"E63"),sQuery(id+"F38.wireOp",EDGE,"E66"),sQuery(id+"F41.wireOp",EDGE,"E67"),sQuery(id+"F51.wireOp",EDGE,"E75"),subQ0,sQuery(id+"F54.wireOp",EDGE,"E79"),sQuery(id+"F54.wireOp",EDGE,"E80")])],"isStart":false}),makeQuery(id+"F56.opExtrude","SWEPT_FACE",FACE,{"disambiguationData":[OSD([subQ0]),TDD([makeQuery(id+"F55.opExtrude","CAP_EDGE",EDGE,{"disambiguationData":[OSD([subQ0])],"isStart":false})])]})]});}
            var sketch = newSketch(context, id + "F57", { "sketchPlane" : qUnion([Q0])});
            skLineSegment(sketch, "E81", {"start": v(-30.56, 102.31) * mm, "end": v(-26.16, 102.31) * mm});
            skSolve(sketch);
        }
        {
            var Q0;
            Q0=qSketchRegion(id+"F57",true);
            var Q1;
            {var subQ0=sQuery(id+"F57.wireOp",EDGE,"E81");Q1=makeQuery(id+"F57.imprint","IMPRINT",FACE,{"disambiguationData":[TD([[makeQuery(id+"F57.imprint","IMPRINT",EDGE,{"derivedFrom":subQ0}),1.0]])]});}
            extrude(context, id + "F58", {"entities" : qUnion([Q0, Q1]), "operationType" : NewBodyOperationType.ADD, "depth" : 4.37 * mm});
        }
        {
            var Q0;
            {var subQ0=sQuery(id+"F54.wireOp",EDGE,"E78");Q0=makeQuery(id+"F58.boolean.opBoolean","MERGE",FACE,{"derivedFrom":[makeQuery(id+"F56.boolean.opBoolean","MERGE",FACE,{"derivedFrom":[makeQuery(id+"F53.opExtrude","CAP_FACE",FACE,{"disambiguationData":[OSD([sQuery(id+"F51.wireOp",EDGE,"E75")])],"isStart":false}),makeQuery(id+"F56.opExtrude","CAP_FACE",FACE,{"disambiguationData":[OSD([subQ0])],"isStart":false})]}),makeQuery(id+"F58.opExtrude","SWEPT_FACE",FACE,{"disambiguationData":[OSD([subQ0])]})]});}
            var sketch = newSketch(context, id + "F59", { "sketchPlane" : qUnion([Q0])});
            skLineSegment(sketch, "E82", {"start": v(-26.16, -39.3) * mm, "end": v(-30.56, -39.3) * mm});
            skSolve(sketch);
        }
        {
            var Q0;
            Q0=qSketchRegion(id+"F59",true);
            var Q1;
            {var subQ0=sQuery(id+"F59.wireOp",EDGE,"E82");Q1=makeQuery(id+"F59.imprint","IMPRINT",FACE,{"disambiguationData":[TD([[makeQuery(id+"F59.imprint","IMPRINT",EDGE,{"derivedFrom":subQ0}),1.0]])]});}
            extrude(context, id + "F60", {"entities" : qUnion([Q0, Q1]), "operationType" : NewBodyOperationType.ADD, "depth" : 4.37 * mm});
        }
        {
            var Q0;
            {var subQ0=sQuery(id+"F25.wireOp",EDGE,"E52");Q0=makeQuery(id+"F29.boolean.opBoolean","MERGE",FACE,{"derivedFrom":[makeQuery(id+"F27.opExtrude","CAP_FACE",FACE,{"disambiguationData":[OSD([subQ0])],"isStart":false}),makeQuery(id+"F29.opExtrude","SWEPT_FACE",FACE,{"disambiguationData":[OSD([subQ0])]})]});}
            var Q1;
            Q1=makeQuery(id+"F31.opExtrude","CAP_FACE",FACE,{"disambiguationData":[OSD([sQuery(id+"F25.wireOp",EDGE,"E51"),sQuery(id+"F25.wireOp",EDGE,"E52"),sQuery(id+"F25.wireOp",EDGE,"E53"),sQuery(id+"F30.wireOp",EDGE,"E57")])],"isStart":false});
            var Q2;
            Q2=makeQuery(id+"F34.opExtrude","CAP_FACE",FACE,{"disambiguationData":[OSD([sQuery(id+"F32.wireOp",EDGE,"E58")])],"isStart":false});
            var Q3;
            Q3=makeQuery(id+"F37.opExtrude","CAP_FACE",FACE,{"disambiguationData":[OSD([sQuery(id+"F35.wireOp",EDGE,"E63")])],"isStart":false});
            var Q4;
            Q4=makeQuery(id+"F40.opExtrude","CAP_FACE",FACE,{"disambiguationData":[OSD([sQuery(id+"F38.wireOp",EDGE,"E66")])],"isStart":false});
            var Q5;
            Q5=makeQuery(id+"F50.opExtrude","CAP_FACE",FACE,{"disambiguationData":[OSD([sQuery(id+"F41.wireOp",EDGE,"E67")])],"isStart":false});
            var Q6;
            {var subQ0=sQuery(id+"F54.wireOp",EDGE,"E78");Q6=makeQuery(id+"F58.boolean.opBoolean","MERGE",FACE,{"derivedFrom":[makeQuery(id+"F56.boolean.opBoolean","MERGE",FACE,{"derivedFrom":[makeQuery(id+"F53.opExtrude","CAP_FACE",FACE,{"disambiguationData":[OSD([sQuery(id+"F51.wireOp",EDGE,"E75")])],"isStart":false}),makeQuery(id+"F56.opExtrude","CAP_FACE",FACE,{"disambiguationData":[OSD([subQ0])],"isStart":false})]}),makeQuery(id+"F58.opExtrude","SWEPT_FACE",FACE,{"disambiguationData":[OSD([subQ0])]})]});}
            var Q7;
            Q7=makeQuery(id+"F60.opExtrude","CAP_FACE",FACE,{"disambiguationData":[OSD([sQuery(id+"F25.wireOp",EDGE,"E51"),sQuery(id+"F25.wireOp",EDGE,"E52"),sQuery(id+"F25.wireOp",EDGE,"E53"),sQuery(id+"F32.wireOp",EDGE,"E58"),sQuery(id+"F32.wireOp",EDGE,"E59"),sQuery(id+"F35.wireOp",EDGE,"E62"),sQuery(id+"F35.wireOp",EDGE,"E63"),sQuery(id+"F38.wireOp",EDGE,"E65"),sQuery(id+"F38.wireOp",EDGE,"E66"),sQuery(id+"F41.wireOp",EDGE,"E67"),sQuery(id+"F41.wireOp",EDGE,"E68"),sQuery(id+"F51.wireOp",EDGE,"E75"),sQuery(id+"F51.wireOp",EDGE,"E76"),sQuery(id+"F54.wireOp",EDGE,"E78"),sQuery(id+"F54.wireOp",EDGE,"E79"),sQuery(id+"F59.wireOp",EDGE,"E82")])],"isStart":false});
            extrude(context, id + "F61", {"entities" : qUnion([Q0, Q1, Q2, Q3, Q4, Q5, Q6, Q7]), "operationType" : NewBodyOperationType.ADD, "depth" : 4.37 * mm});
        }
        {
            var Q0;
            {var subQ0=sQuery(id+"F25.wireOp",EDGE,"E52");Q0=makeQuery(id+"F61.boolean.opBoolean","MERGE",FACE,{"derivedFrom":[makeQuery(id+"F31.opExtrude","CAP_FACE",FACE,{"disambiguationData":[OSD([sQuery(id+"F25.wireOp",EDGE,"E51"),subQ0,sQuery(id+"F25.wireOp",EDGE,"E53"),sQuery(id+"F30.wireOp",EDGE,"E57")])],"isStart":false}),makeQuery(id+"F61.opExtrude","CAP_FACE",FACE,{"disambiguationData":[OSD([subQ0])],"isStart":false})]});}
            var Q1;
            Q1=makeQuery(id+"F61.opExtrude","CAP_FACE",FACE,{"disambiguationData":[OSD([sQuery(id+"F25.wireOp",EDGE,"E51"),sQuery(id+"F25.wireOp",EDGE,"E52"),sQuery(id+"F25.wireOp",EDGE,"E53"),sQuery(id+"F30.wireOp",EDGE,"E57")])],"isStart":false});
            var Q2;
            Q2=makeQuery(id+"F61.boolean.opBoolean","MERGE",FACE,{"derivedFrom":[makeQuery(id+"F37.opExtrude","CAP_FACE",FACE,{"disambiguationData":[OSD([sQuery(id+"F35.wireOp",EDGE,"E63")])],"isStart":false}),makeQuery(id+"F61.opExtrude","CAP_FACE",FACE,{"disambiguationData":[OSD([sQuery(id+"F32.wireOp",EDGE,"E58")])],"isStart":false})]});
            var Q3;
            Q3=makeQuery(id+"F61.boolean.opBoolean","MERGE",FACE,{"derivedFrom":[makeQuery(id+"F40.opExtrude","CAP_FACE",FACE,{"disambiguationData":[OSD([sQuery(id+"F38.wireOp",EDGE,"E66")])],"isStart":false}),makeQuery(id+"F61.opExtrude","CAP_FACE",FACE,{"disambiguationData":[OSD([sQuery(id+"F35.wireOp",EDGE,"E63")])],"isStart":false})]});
            var Q4;
            Q4=makeQuery(id+"F61.boolean.opBoolean","MERGE",FACE,{"derivedFrom":[makeQuery(id+"F50.opExtrude","CAP_FACE",FACE,{"disambiguationData":[OSD([sQuery(id+"F41.wireOp",EDGE,"E67")])],"isStart":false}),makeQuery(id+"F61.opExtrude","CAP_FACE",FACE,{"disambiguationData":[OSD([sQuery(id+"F38.wireOp",EDGE,"E66")])],"isStart":false})]});
            var Q5;
            Q5=makeQuery(id+"F61.opExtrude","CAP_FACE",FACE,{"disambiguationData":[OSD([sQuery(id+"F41.wireOp",EDGE,"E67")])],"isStart":false});
            var Q6;
            {var subQ0=sQuery(id+"F54.wireOp",EDGE,"E78");var subQ1=sQuery(id+"F51.wireOp",EDGE,"E75");Q6=makeQuery(id+"F61.boolean.opBoolean","MERGE",FACE,{"derivedFrom":[makeQuery(id+"F60.opExtrude","CAP_FACE",FACE,{"disambiguationData":[OSD([sQuery(id+"F25.wireOp",EDGE,"E51"),sQuery(id+"F25.wireOp",EDGE,"E52"),sQuery(id+"F25.wireOp",EDGE,"E53"),sQuery(id+"F32.wireOp",EDGE,"E58"),sQuery(id+"F32.wireOp",EDGE,"E59"),sQuery(id+"F35.wireOp",EDGE,"E62"),sQuery(id+"F35.wireOp",EDGE,"E63"),sQuery(id+"F38.wireOp",EDGE,"E65"),sQuery(id+"F38.wireOp",EDGE,"E66"),sQuery(id+"F41.wireOp",EDGE,"E67"),sQuery(id+"F41.wireOp",EDGE,"E68"),subQ1,sQuery(id+"F51.wireOp",EDGE,"E76"),subQ0,sQuery(id+"F54.wireOp",EDGE,"E79"),sQuery(id+"F59.wireOp",EDGE,"E82")])],"isStart":false}),makeQuery(id+"F61.opExtrude","CAP_FACE",FACE,{"disambiguationData":[OSD([subQ1,subQ0])],"isStart":false})]});}
            extrude(context, id + "F62", {"entities" : qUnion([Q0, Q1, Q2, Q3, Q4, Q5, Q6]), "operationType" : NewBodyOperationType.ADD, "depth" : 4.37 * mm});
        }
        {
            var Q0;
            Q0=makeQuery(id+"F29.opExtrude","SWEPT_FACE",FACE,{"disambiguationData":[OSD([sQuery(id+"F28.wireOp",EDGE,"E55")])]});
            extrude(context, id + "F63", {"entities" : qUnion([Q0]), "operationType" : NewBodyOperationType.ADD, "depth" : 4.37 * mm});
        }
        {
            var Q0;
            {var subQ0=sQuery(id+"F17.wireOp",EDGE,"E21");Q0=makeQuery(id+"F63.boolean.opBoolean","MERGE",FACE,{"derivedFrom":[makeQuery(id+"F44.boolean.opBoolean","MERGE",FACE,{"derivedFrom":[makeQuery(id+"F26.boolean.opBoolean","MERGE",FACE,{"derivedFrom":[makeQuery(id+"F23.boolean.opBoolean","MERGE",FACE,{"derivedFrom":[makeQuery(id+"F16.opExtrude","SWEPT_FACE",FACE,{"disambiguationData":[OSD([sQuery(id+"F15.wireOp",EDGE,"E9")])]}),makeQuery(id+"F23.opExtrude","SWEPT_FACE",FACE,{"disambiguationData":[OSD([subQ0])]})]}),makeQuery(id+"F26.opExtrude","SWEPT_FACE",FACE,{"disambiguationData":[OSD([sQuery(id+"F25.wireOp",EDGE,"E54")])]})]}),makeQuery(id+"F44.opExtrude","SWEPT_FACE",FACE,{"disambiguationData":[OSD([subQ0])]})]}),makeQuery(id+"F63.opExtrude","CAP_FACE",FACE,{"disambiguationData":[OSD([sQuery(id+"F28.wireOp",EDGE,"E55")])],"isStart":false})]});}
            var sketch = newSketch(context, id + "F64", { "sketchPlane" : qUnion([Q0])});
            skLineSegment(sketch, "E83", {"start": v(-17.46, 8.73) * mm, "end": v(-34.92, 8.73) * mm});
            skSolve(sketch);
        }
        {
            var Q0;
            Q0=qSketchRegion(id+"F64",true);
            var Q1;
            {var subQ1=sQuery(id+"F28.wireOp",EDGE,"E55");Q1=makeQuery(id+"F64.imprint","IMPRINT",FACE,{"disambiguationData":[TD([[makeQuery(id+"F64.imprint","IMPRINT",EDGE,{"derivedFrom":makeQuery(id+"F63.opExtrude","CAP_EDGE",EDGE,{"disambiguationData":[OSD([subQ1]),TDD([makeQuery(id+"F29.opExtrude","CAP_EDGE",EDGE,{"disambiguationData":[OSD([subQ1])],"isStart":false})])],"isStart":false})}),-1.0]])]});}
            extrude(context, id + "F65", {"entities" : qUnion([Q0, Q1]), "operationType" : NewBodyOperationType.ADD, "depth" : 4.37 * mm});
        }
        {
            var Q0;
            {var subQ0=sQuery(id+"F28.wireOp",EDGE,"E55");var subQ1=sQuery(id+"F25.wireOp",EDGE,"E53");var subQ2=sQuery(id+"F25.wireOp",EDGE,"E52");var subQ3=sQuery(id+"F25.wireOp",EDGE,"E51");Q0=makeQuery(id+"F65.boolean.opBoolean","MERGE",FACE,{"derivedFrom":[makeQuery(id+"F63.boolean.opBoolean","MERGE",FACE,{"derivedFrom":[makeQuery(id+"F33.boolean.opBoolean","SPLIT",FACE,{"disambiguationData":[TD([makeQuery(id+"F29.opExtrude","SWEPT_FACE",FACE,{"disambiguationData":[OSD([subQ0])]})])],"derivedFrom":makeQuery(id+"F31.boolean.opBoolean","MERGE",FACE,{"derivedFrom":[makeQuery(id+"F29.opExtrude","CAP_FACE",FACE,{"disambiguationData":[OSD([subQ3,subQ2,subQ1,subQ0])],"isStart":false}),makeQuery(id+"F31.opExtrude","SWEPT_FACE",FACE,{"disambiguationData":[OSD([subQ2])]})]})}),makeQuery(id+"F63.opExtrude","SWEPT_FACE",FACE,{"disambiguationData":[OSD([subQ0]),TDD([makeQuery(id+"F29.opExtrude","CAP_EDGE",EDGE,{"disambiguationData":[OSD([subQ0])],"isStart":false})])]})]}),makeQuery(id+"F65.opExtrude","SWEPT_FACE",FACE,{"disambiguationData":[OSD([subQ0])]})]});}
            var sketch = newSketch(context, id + "F66", { "sketchPlane" : qUnion([Q0])});
            skLineSegment(sketch, "E84", {"start": v(-26.16, 71.75) * mm, "end": v(-30.56, 71.75) * mm});
            skLineSegment(sketch, "E85", {"start": v(-30.56, 71.75) * mm, "end": v(-30.56, 67.39) * mm});
            skLineSegment(sketch, "E86", {"start": v(-30.56, 67.39) * mm, "end": v(-26.16, 67.39) * mm});
            skSolve(sketch);
        }
        {
            var Q0;
            Q0=qSketchRegion(id+"F66",true);
            var Q1;
            {var subQ0=sQuery(id+"F66.wireOp",EDGE,"E84");Q1=makeQuery(id+"F66.imprint","IMPRINT",FACE,{"disambiguationData":[TD([[makeQuery(id+"F66.imprint","IMPRINT",EDGE,{"derivedFrom":subQ0}),1.0]])]});}
            var Q2;
            {var subQ0=sQuery(id+"F66.wireOp",EDGE,"E86");Q2=makeQuery(id+"F66.imprint","IMPRINT",FACE,{"disambiguationData":[TD([[makeQuery(id+"F66.imprint","IMPRINT",EDGE,{"derivedFrom":subQ0}),-1.0]])]});}
            extrude(context, id + "F67", {"entities" : qUnion([Q0, Q1, Q2]), "operationType" : NewBodyOperationType.ADD, "depth" : 4.37 * mm});
        }
        {
            var Q0;
            {var subQ0=sQuery(id+"F28.wireOp",EDGE,"E55");Q0=makeQuery(id+"F67.boolean.opBoolean","MERGE",FACE,{"derivedFrom":[makeQuery(id+"F65.opExtrude","CAP_FACE",FACE,{"disambiguationData":[OSD([sQuery(id+"F25.wireOp",EDGE,"E47"),sQuery(id+"F25.wireOp",EDGE,"E51"),sQuery(id+"F25.wireOp",EDGE,"E52"),sQuery(id+"F25.wireOp",EDGE,"E53"),sQuery(id+"F25.wireOp",EDGE,"E54"),subQ0,sQuery(id+"F64.wireOp",EDGE,"E83")])],"isStart":false}),makeQuery(id+"F67.opExtrude","SWEPT_FACE",FACE,{"disambiguationData":[OSD([subQ0])]})]});}
            var sketch = newSketch(context, id + "F68", { "sketchPlane" : qUnion([Q0])});
            skLineSegment(sketch, "E87", {"start": v(-30.56, 17.46) * mm, "end": v(-26.16, 17.46) * mm});
            skSolve(sketch);
        }
        {
            var Q0;
            Q0=qSketchRegion(id+"F68",true);
            var Q1;
            {var subQ0=sQuery(id+"F68.wireOp",EDGE,"E87");Q1=makeQuery(id+"F68.imprint","IMPRINT",FACE,{"disambiguationData":[TD([[makeQuery(id+"F68.imprint","IMPRINT",EDGE,{"derivedFrom":subQ0}),1.0]])]});}
            extrude(context, id + "F69", {"entities" : qUnion([Q0, Q1]), "operationType" : NewBodyOperationType.ADD, "depth" : 4.37 * mm});
        }
        {
            var Q0;
            {var subQ0=sQuery(id+"F28.wireOp",EDGE,"E55");Q0=makeQuery(id+"F69.boolean.opBoolean","MERGE",FACE,{"derivedFrom":[makeQuery(id+"F67.opExtrude","CAP_FACE",FACE,{"disambiguationData":[OSD([sQuery(id+"F25.wireOp",EDGE,"E47"),sQuery(id+"F25.wireOp",EDGE,"E51"),sQuery(id+"F25.wireOp",EDGE,"E52"),sQuery(id+"F25.wireOp",EDGE,"E53"),sQuery(id+"F25.wireOp",EDGE,"E54"),subQ0,sQuery(id+"F66.wireOp",EDGE,"E84"),sQuery(id+"F66.wireOp",EDGE,"E85")])],"isStart":false}),makeQuery(id+"F69.opExtrude","SWEPT_FACE",FACE,{"disambiguationData":[OSD([subQ0])]})]});}
            var sketch = newSketch(context, id + "F70", { "sketchPlane" : qUnion([Q0])});
            skLineSegment(sketch, "E88", {"start": v(-30.56, 67) * mm, "end": v(-26.16, 67) * mm});
            skLineSegment(sketch, "E89", {"start": v(-26.16, 67) * mm, "end": v(-26.16, 62.57) * mm});
            skLineSegment(sketch, "E90", {"start": v(-26.16, 62.57) * mm, "end": v(-30.56, 62.57) * mm});
            skSolve(sketch);
        }
        {
            var Q0;
            {var subQ0=sQuery(id+"F70.wireOp",EDGE,"E88");Q0=makeQuery(id+"F70.imprint","IMPRINT",FACE,{"disambiguationData":[TD([[makeQuery(id+"F70.imprint","IMPRINT",EDGE,{"derivedFrom":subQ0}),-1.0]])]});}
            var Q1;
            {var subQ0=sQuery(id+"F70.wireOp",EDGE,"E90");Q1=makeQuery(id+"F70.imprint","IMPRINT",FACE,{"disambiguationData":[TD([[makeQuery(id+"F70.imprint","IMPRINT",EDGE,{"derivedFrom":subQ0}),1.0]])]});}
            extrude(context, id + "F71", {"entities" : qUnion([Q0, Q1]), "operationType" : NewBodyOperationType.ADD, "depth" : 4.36 * mm});
        }
        {
            var Q0;
            Q0=makeQuery(id+"F21.imprint","IMPRINT",FACE,{"disambiguationData":[TD([[makeQuery(id+"F21.imprint","IMPRINT",EDGE,{"derivedFrom":sQuery(id+"F21.wireOp",EDGE,"E43")}),-1.0]])]});
            var Q1;
            Q1=sQuery(id+"F21.wireOp",EDGE,"E43");
            var Q2;
            Q2=sQuery(id+"F21.wireOp",EDGE,"E45");
            var Q3;
            Q3=sQuery(id+"F21.wireOp",EDGE,"E44");
            var Q4;
            Q4=sQuery(id+"F21.wireOp",EDGE,"E46");
            extrude(context, id + "F72", {"entities" : qUnion([Q0]), "operationType" : NewBodyOperationType.REMOVE, "surfaceEntities" : qUnion([Q1, Q2, Q3, Q4]), "oppositeDirection" : true, "depth" : 4.37 * mm});
        }
    });
